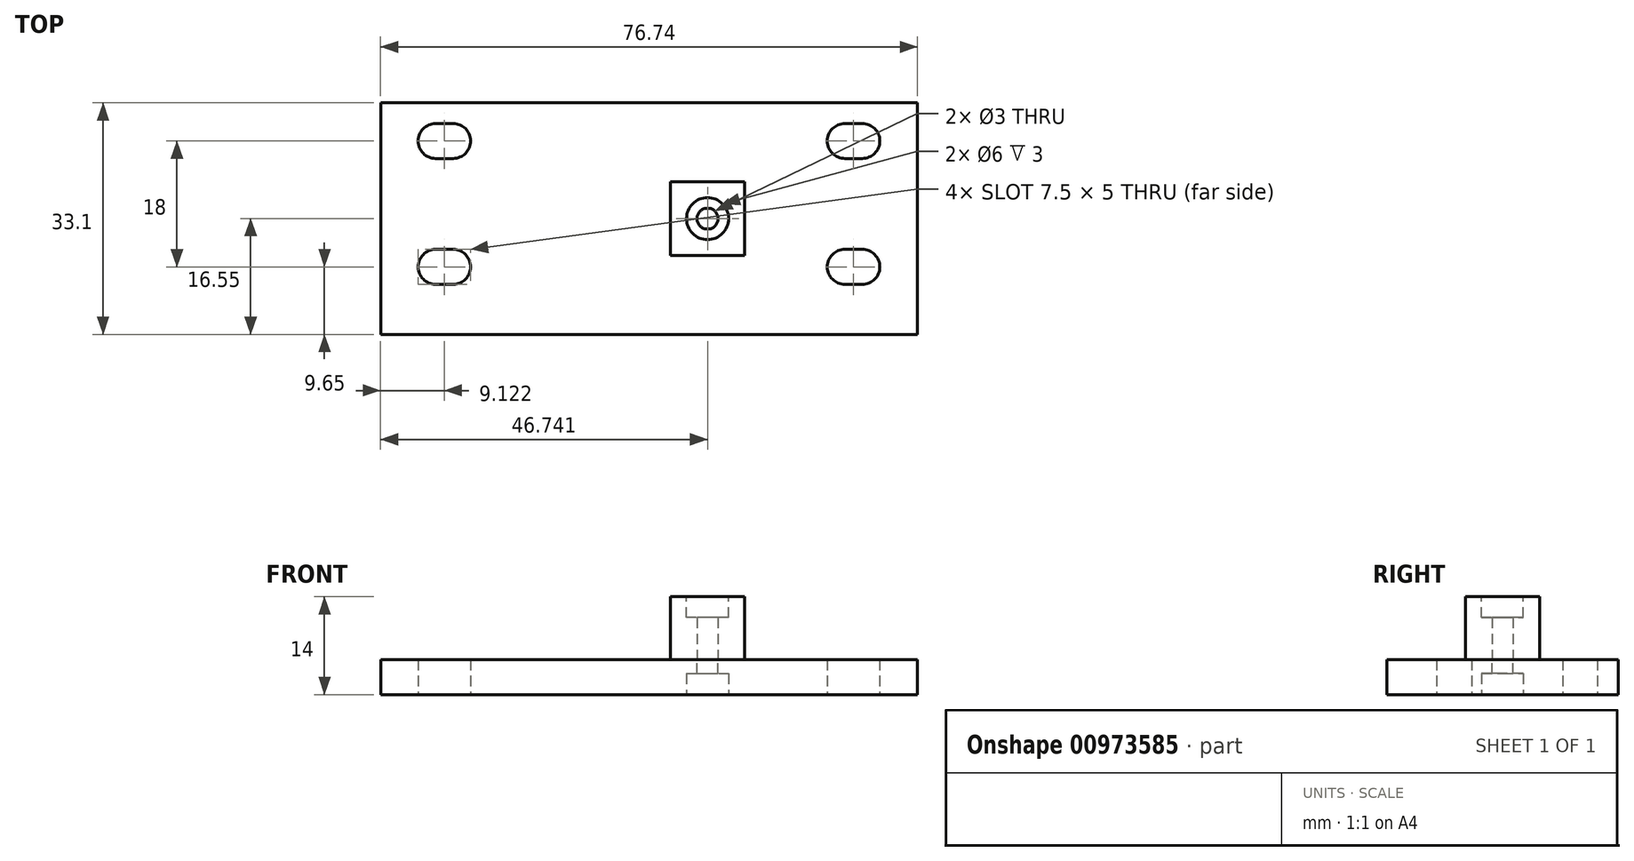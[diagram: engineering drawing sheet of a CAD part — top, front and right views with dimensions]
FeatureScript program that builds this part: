
annotation { "Feature Type Name" : "Feature", "Feature Type Description" : "" }
export const myFeature = defineFeature(function(context is Context, id is Id, definition is map)
    precondition{}
    {
        {
            var Q0;
            Q0=qCreatedBy(makeId("Front.planeOp"),FACE);
            var sketch = newSketch(context, id + "F0", { "sketchPlane" : qUnion([Q0])});
            skCircle(sketch, "E0", {"center": v(17.73, -4.86) * mm, "radius": 4 * mm});
            skLineSegment(sketch, "E1.bottom", {"start": v(0.73, 6.14) * mm, "end": v(34.73, 6.14) * mm});
            skLineSegment(sketch, "E1.top", {"start": v(0.73, -15.86) * mm, "end": v(34.73, -15.86) * mm});
            skLineSegment(sketch, "E1.left", {"start": v(0.73, 6.14) * mm, "end": v(0.73, -15.86) * mm});
            skLineSegment(sketch, "E1.right", {"start": v(34.73, 6.14) * mm, "end": v(34.73, -15.86) * mm});
            skPoint(sketch, "E2.MirrorP", {"position": v(-19.07, -4.86) * mm});
            skLineSegment(sketch, "E3.MirrorCS", {"start": v(-2.07, 6.14) * mm, "end": v(-2.07, -15.86) * mm});
            skLineSegment(sketch, "E4.MirrorCS", {"start": v(-2.07, 6.14) * mm, "end": v(-36.07, 6.14) * mm});
            skLineSegment(sketch, "E5.MirrorCS", {"start": v(-2.07, -15.86) * mm, "end": v(-36.07, -15.86) * mm});
            skLineSegment(sketch, "E6.MirrorCS", {"start": v(-36.07, 6.14) * mm, "end": v(-36.07, -15.86) * mm});
            skCircle(sketch, "E7.MirrorC", {"center": v(-19.07, -4.86) * mm, "radius": 4 * mm});
            skPoint(sketch, "E8.MirrorCS.start.orphan", {"position": v(-19.07, 25.28) * mm});
            skPoint(sketch, "E9.orphan", {"position": v(-23.47, 25.28) * mm});
            skPoint(sketch, "E10.MirrorCS.end.orphan", {"position": v(-23.47, -17.2) * mm});
            skPoint(sketch, "E11.orphan", {"position": v(-19.07, -16.86) * mm});
            skPoint(sketch, "E12.orphan", {"position": v(17.73, -16.86) * mm});
            skPoint(sketch, "E13.orphan", {"position": v(22.13, -17.2) * mm});
            skPoint(sketch, "E14.start.orphan", {"position": v(17.73, 25.28) * mm});
            skPoint(sketch, "E15.orphan", {"position": v(13.33, 25.28) * mm});
            skPoint(sketch, "E16.end.orphan", {"position": v(22.13, 25.28) * mm});
            skSolve(sketch);
        }
        {
            var Q0;
            Q0=makeQuery(id+"F0.imprint","IMPRINT",FACE,{"disambiguationData":[TD([[makeQuery(id+"F0.imprint","IMPRINT",EDGE,{"derivedFrom":sQuery(id+"F0.wireOp",EDGE,"E3.MirrorCS")}),-1.0]])]});
            var Q1;
            Q1=makeQuery(id+"F0.imprint","IMPRINT",FACE,{"disambiguationData":[TD([[makeQuery(id+"F0.imprint","IMPRINT",EDGE,{"derivedFrom":sQuery(id+"F0.wireOp",EDGE,"E0")}),-1.0]])]});
            extrude(context, id + "F1", {"entities" : qUnion([Q0, Q1]), "depth" : 30.2 * mm, "offsetDistance" : 25 * mm});
        }
        {
            var Q0;
            Q0=makeQuery(id+"F1.opExtrude","SWEPT_FACE",FACE,{"disambiguationData":[OSD([sQuery(id+"F0.wireOp",EDGE,"E1.bottom")])]});
            var sketch = newSketch(context, id + "F2", { "sketchPlane" : qUnion([Q0])});
            skArc(sketch, "E17", {"start": v(27.95, -24.5) * mm, "mid": v(30.45, -22) * mm, "end": v(27.95, -19.5) * mm});
            skArc(sketch, "E18.MirrorC", {"start": v(-33.05, -6.5) * mm, "mid": v(-35.55, -4) * mm, "end": v(-33.05, -1.5) * mm});
            skArc(sketch, "E19.MirrorC", {"start": v(-33.05, -24.5) * mm, "mid": v(-35.55, -22) * mm, "end": v(-33.05, -19.5) * mm});
            skLineSegment(sketch, "E20.bottom", {"start": v(-40.92, 1.45) * mm, "end": v(35.82, 1.45) * mm});
            skLineSegment(sketch, "E20.top", {"start": v(-40.92, -31.65) * mm, "end": v(35.82, -31.65) * mm});
            skLineSegment(sketch, "E20.left", {"start": v(-40.92, 1.45) * mm, "end": v(-40.92, -31.65) * mm});
            skLineSegment(sketch, "E20.right", {"start": v(35.82, 1.45) * mm, "end": v(35.82, -31.65) * mm});
            skLineSegment(sketch, "E21", {"start": v(-2.55, 1.45) * mm, "end": v(-2.55, 6.82) * mm});
            skArc(sketch, "E22", {"start": v(-30.55, -6.5) * mm, "mid": v(-28.05, -4) * mm, "end": v(-30.55, -1.5) * mm});
            skArc(sketch, "E23", {"start": v(-30.55, -24.5) * mm, "mid": v(-28.05, -22) * mm, "end": v(-30.55, -19.5) * mm});
            skArc(sketch, "E24.MirrorC", {"start": v(25.45, -24.5) * mm, "mid": v(22.95, -22) * mm, "end": v(25.45, -19.5) * mm});
            skLineSegment(sketch, "E25", {"start": v(-33.05, -1.5) * mm, "end": v(-30.55, -1.5) * mm});
            skLineSegment(sketch, "E26.MirrorCS", {"start": v(-33.05, -6.5) * mm, "end": v(-30.55, -6.5) * mm});
            skLineSegment(sketch, "E27", {"start": v(-33.05, -19.5) * mm, "end": v(-30.55, -19.5) * mm});
            skLineSegment(sketch, "E28.MirrorCS", {"start": v(-33.05, -24.5) * mm, "end": v(-30.55, -24.5) * mm});
            skLineSegment(sketch, "E29.MirrorCS", {"start": v(27.95, -1.5) * mm, "end": v(25.45, -1.5) * mm});
            skLineSegment(sketch, "E30.MirrorCS", {"start": v(27.95, -6.5) * mm, "end": v(25.45, -6.5) * mm});
            skLineSegment(sketch, "E31.MirrorCS", {"start": v(27.95, -19.5) * mm, "end": v(25.45, -19.5) * mm});
            skLineSegment(sketch, "E32.MirrorCS", {"start": v(27.95, -24.5) * mm, "end": v(25.45, -24.5) * mm});
            skArc(sketch, "E33.trimOffspring", {"start": v(25.45, -6.5) * mm, "mid": v(22.95, -4) * mm, "end": v(25.45, -1.5) * mm});
            skArc(sketch, "E34.trimOffspring", {"start": v(27.95, -6.5) * mm, "mid": v(30.45, -4) * mm, "end": v(27.95, -1.5) * mm});
            skSolve(sketch);
        }
        {
            var Q0;
            Q0=qSketchRegion(id+"F2",true);
            extrude(context, id + "F3", {"entities" : qUnion([Q0]), "depth" : 5 * mm, "offsetDistance" : 25 * mm});
        }
        {
            var Q0;
            Q0=makeQuery(id+"F1.opExtrude","SWEPT_BODY",BODY,{"disambiguationData":[OSD([sQuery(id+"F0.wireOp",EDGE,"E3.MirrorCS"),sQuery(id+"F0.wireOp",EDGE,"E4.MirrorCS"),sQuery(id+"F0.wireOp",EDGE,"E5.MirrorCS"),sQuery(id+"F0.wireOp",EDGE,"E6.MirrorCS"),sQuery(id+"F0.wireOp",EDGE,"E7.MirrorC")])]});
            deleteBodies(context, id + "F4", {"entities" : qUnion([Q0])});
        }
        {
            var Q0;
            Q0=makeQuery(id+"F1.opExtrude","SWEPT_BODY",BODY,{"disambiguationData":[OSD([sQuery(id+"F0.wireOp",EDGE,"E0"),sQuery(id+"F0.wireOp",EDGE,"E1.bottom"),sQuery(id+"F0.wireOp",EDGE,"E1.top"),sQuery(id+"F0.wireOp",EDGE,"E1.left"),sQuery(id+"F0.wireOp",EDGE,"E1.right")])]});
            deleteBodies(context, id + "F5", {"entities" : qUnion([Q0])});
        }
        {
            var Q0;
            Q0=makeQuery(id+"F3.opExtrude","CAP_FACE",FACE,{"disambiguationData":[OSD([sQuery(id+"F2.wireOp",EDGE,"E17"),sQuery(id+"F2.wireOp",EDGE,"E18.MirrorC"),sQuery(id+"F2.wireOp",EDGE,"E19.MirrorC"),sQuery(id+"F2.wireOp",EDGE,"E20.bottom"),sQuery(id+"F2.wireOp",EDGE,"E20.top"),sQuery(id+"F2.wireOp",EDGE,"E20.left"),sQuery(id+"F2.wireOp",EDGE,"E20.right"),sQuery(id+"F2.wireOp",EDGE,"E22"),sQuery(id+"F2.wireOp",EDGE,"E23"),sQuery(id+"F2.wireOp",EDGE,"E24.MirrorC"),sQuery(id+"F2.wireOp",EDGE,"E25"),sQuery(id+"F2.wireOp",EDGE,"E26.MirrorCS"),sQuery(id+"F2.wireOp",EDGE,"E27"),sQuery(id+"F2.wireOp",EDGE,"E28.MirrorCS"),sQuery(id+"F2.wireOp",EDGE,"E29.MirrorCS"),sQuery(id+"F2.wireOp",EDGE,"E30.MirrorCS"),sQuery(id+"F2.wireOp",EDGE,"E31.MirrorCS"),sQuery(id+"F2.wireOp",EDGE,"E32.MirrorCS"),sQuery(id+"F2.wireOp",EDGE,"E33.trimOffspring"),sQuery(id+"F2.wireOp",EDGE,"E34.trimOffspring")])],"isStart":false});
            var sketch = newSketch(context, id + "F6", { "sketchPlane" : qUnion([Q0])});
            skCircle(sketch, "E35", {"center": v(5.82, -15.1) * mm, "radius": 1.5 * mm});
            skPoint(sketch, "E36.orphan", {"position": v(5.82, -31.65) * mm});
            skPoint(sketch, "E37.orphan", {"position": v(35.82, -15.1) * mm});
            skSolve(sketch);
        }
        {
            var Q0;
            Q0 = qSketchRegion(id + "F6", true);
            extrude(context, id + "F7", {"entities" : qUnion([Q0]), "operationType" : NewBodyOperationType.REMOVE, "oppositeDirection" : true, "depth" : 25 * mm, "offsetDistance" : 25 * mm});
        }
        {
            var Q0;
            Q0=makeQuery(id+"F3.opExtrude","CAP_FACE",FACE,{"disambiguationData":[OSD([sQuery(id+"F2.wireOp",EDGE,"E17"),sQuery(id+"F2.wireOp",EDGE,"E18.MirrorC"),sQuery(id+"F2.wireOp",EDGE,"E19.MirrorC"),sQuery(id+"F2.wireOp",EDGE,"E20.bottom"),sQuery(id+"F2.wireOp",EDGE,"E20.top"),sQuery(id+"F2.wireOp",EDGE,"E20.left"),sQuery(id+"F2.wireOp",EDGE,"E20.right"),sQuery(id+"F2.wireOp",EDGE,"E22"),sQuery(id+"F2.wireOp",EDGE,"E23"),sQuery(id+"F2.wireOp",EDGE,"E24.MirrorC"),sQuery(id+"F2.wireOp",EDGE,"E25"),sQuery(id+"F2.wireOp",EDGE,"E26.MirrorCS"),sQuery(id+"F2.wireOp",EDGE,"E27"),sQuery(id+"F2.wireOp",EDGE,"E28.MirrorCS"),sQuery(id+"F2.wireOp",EDGE,"E29.MirrorCS"),sQuery(id+"F2.wireOp",EDGE,"E30.MirrorCS"),sQuery(id+"F2.wireOp",EDGE,"E31.MirrorCS"),sQuery(id+"F2.wireOp",EDGE,"E32.MirrorCS"),sQuery(id+"F2.wireOp",EDGE,"E33.trimOffspring"),sQuery(id+"F2.wireOp",EDGE,"E34.trimOffspring")])],"isStart":true});
            var sketch = newSketch(context, id + "F8", { "sketchPlane" : qUnion([Q0])});
            skCircle(sketch, "E38", {"center": v(5.82, 15.1) * mm, "radius": 3 * mm});
            skSolve(sketch);
        }
        {
            var Q0;
            Q0 = qSketchRegion(id + "F8", true);
            extrude(context, id + "F9", {"entities" : qUnion([Q0]), "operationType" : NewBodyOperationType.REMOVE, "oppositeDirection" : true, "depth" : 3 * mm, "offsetDistance" : 25 * mm});
        }
        {
            var Q0;
            Q0=makeQuery(id+"F3.opExtrude","CAP_FACE",FACE,{"disambiguationData":[OSD([sQuery(id+"F2.wireOp",EDGE,"E17"),sQuery(id+"F2.wireOp",EDGE,"E18.MirrorC"),sQuery(id+"F2.wireOp",EDGE,"E19.MirrorC"),sQuery(id+"F2.wireOp",EDGE,"E20.bottom"),sQuery(id+"F2.wireOp",EDGE,"E20.top"),sQuery(id+"F2.wireOp",EDGE,"E20.left"),sQuery(id+"F2.wireOp",EDGE,"E20.right"),sQuery(id+"F2.wireOp",EDGE,"E22"),sQuery(id+"F2.wireOp",EDGE,"E23"),sQuery(id+"F2.wireOp",EDGE,"E24.MirrorC"),sQuery(id+"F2.wireOp",EDGE,"E25"),sQuery(id+"F2.wireOp",EDGE,"E26.MirrorCS"),sQuery(id+"F2.wireOp",EDGE,"E27"),sQuery(id+"F2.wireOp",EDGE,"E28.MirrorCS"),sQuery(id+"F2.wireOp",EDGE,"E29.MirrorCS"),sQuery(id+"F2.wireOp",EDGE,"E30.MirrorCS"),sQuery(id+"F2.wireOp",EDGE,"E31.MirrorCS"),sQuery(id+"F2.wireOp",EDGE,"E32.MirrorCS"),sQuery(id+"F2.wireOp",EDGE,"E33.trimOffspring"),sQuery(id+"F2.wireOp",EDGE,"E34.trimOffspring")])],"isStart":false});
            var sketch = newSketch(context, id + "F10", { "sketchPlane" : qUnion([Q0])});
            skLineSegment(sketch, "E39.bottom", {"start": v(11.12, -9.8) * mm, "end": v(0.52, -9.8) * mm});
            skLineSegment(sketch, "E39.top", {"start": v(11.12, -20.4) * mm, "end": v(0.52, -20.4) * mm});
            skLineSegment(sketch, "E39.left", {"start": v(11.12, -9.8) * mm, "end": v(11.12, -20.4) * mm});
            skLineSegment(sketch, "E39.right", {"start": v(0.52, -9.8) * mm, "end": v(0.52, -20.4) * mm});
            skPoint(sketch, "E39.middle", {"position": v(5.82, -15.1) * mm});
            skCircle(sketch, "E40", {"center": v(5.82, -15.1) * mm, "radius": 1.5 * mm});
            skSolve(sketch);
        }
        {
            var Q0;
            Q0 = qSketchRegion(id + "F10", true);
            extrude(context, id + "F11", {"entities" : qUnion([Q0]), "depth" : 9 * mm, "offsetDistance" : 25 * mm});
        }
        {
            var Q0;
            Q0=makeQuery(id+"F11.opExtrude","CAP_FACE",FACE,{"disambiguationData":[OSD([sQuery(id+"F10.wireOp",EDGE,"E39.bottom"),sQuery(id+"F10.wireOp",EDGE,"E39.top"),sQuery(id+"F10.wireOp",EDGE,"E39.left"),sQuery(id+"F10.wireOp",EDGE,"E39.right"),sQuery(id+"F10.wireOp",EDGE,"E40")])],"isStart":false});
            var sketch = newSketch(context, id + "F12", { "sketchPlane" : qUnion([Q0])});
            skCircle(sketch, "E41", {"center": v(5.82, -15.1) * mm, "radius": 3 * mm});
            skSolve(sketch);
        }
        {
            var Q0;
            Q0 = qSketchRegion(id + "F12", true);
            extrude(context, id + "F13", {"entities" : qUnion([Q0]), "operationType" : NewBodyOperationType.REMOVE, "oppositeDirection" : true, "depth" : 3 * mm, "offsetDistance" : 25 * mm});
        }
    });
